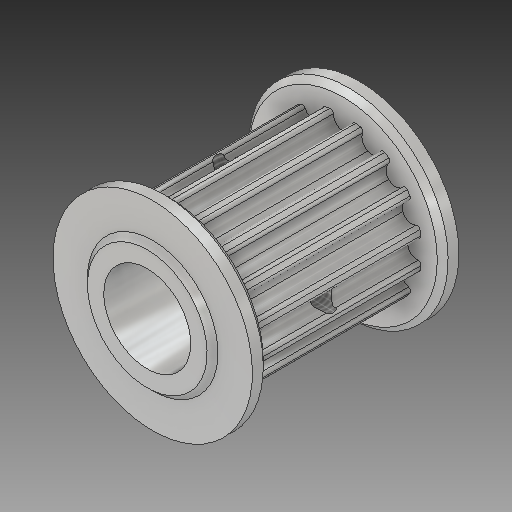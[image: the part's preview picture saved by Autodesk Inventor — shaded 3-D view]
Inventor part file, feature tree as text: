
AUTODESK INVENTOR PART (.ipt)
format: ipt  version: 2019.4 (Build 234330000, 330)  size: 465,920 bytes
history: native  units: mm
features: sketch x4, extrude x3, other x2, plane x2, pattern_circular x2, revolve x1, chamfer x1, mirror x1, thread x1
ambient origin geometry x8: Origin, YZ Plane, XZ Plane, XY Plane, X Axis, Y Axis, Z Axis, Center Point
bodies: Body1 (feature_tree)
feature tree (17):
  other  "gates_P16-3M-09AL.ipt"
  extrude  "Extrusion7"  Depth=10.0mm TaperAngle=0.0deg
  extrude  "Extrusion8"  Depth=15.0mm TaperAngle=0.0deg
  sketch  "Sketch15"  dims[d57=2.0mm d58=1.5mm]
  other  "Work Axis2"
  revolve  "Revolution2"  [1 undecoded]
  chamfer  "Chamfer2"  Distance=0.5mm
  plane  "Work Plane3"
  mirror  "Mirror1"
  plane  "Work Plane4"
  extrude  "Extrusion9"  TaperAngle=90.0deg  [1 undecoded]
  thread  "Thread2"  [1 undecoded]
  pattern_circular  "Circular Pattern1"  [2 undecoded]
  pattern_circular  "Circular Pattern2"  [2 undecoded]
  sketch  "Sketch1"  dims[d51=10.0mm d52=16.0mm d53=0.0mm]
  sketch  "Sketch14"  dims[d54=8.0mm d55=15.0mm d56=0.0mm]
  sketch  "Sketch16"  dims[d59=2.0mm d60=0.5mm d61=90.0deg d62=0.5mm d63=2.0mm d64=45.0deg d65=2.0mm d66=15.0mm d67=0.0mm d68=10.0mm d69=0.0mm d70=20.0mm d71=19.626227mm d73=20.0mm d74=135.0deg]
note: 7 required parameter values undecoded (feature->parameter linkage not recoverable at this tier; creation-order binding heuristic only, values carry confidence <= 0.55)